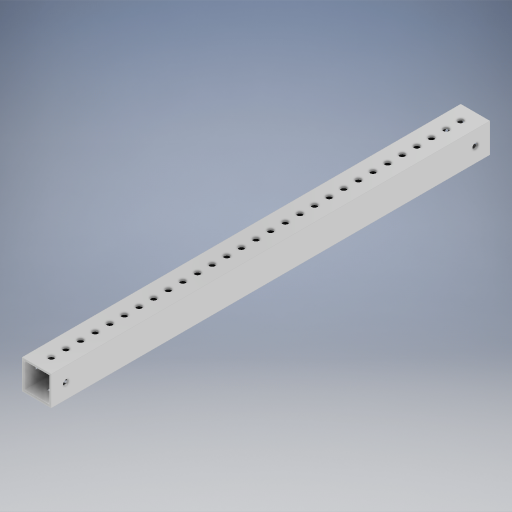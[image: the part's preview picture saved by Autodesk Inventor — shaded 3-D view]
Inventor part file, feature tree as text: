
AUTODESK INVENTOR PART (.ipt)
format: ipt  version: 2024.2 (Build 282272000, 272)  size: 795,136 bytes
history: native  units: in
note: dims shown in document units (in); Inventor stores cm internally (conversion verified against a paired STEP export)
features: other x13, extrude x9, hole x3, pattern_linear x3, mirror x3, sheet_metal_op x1, plane x1
ambient origin geometry x8: Origin, YZ Plane, XZ Plane, XY Plane, X Axis, Y Axis, Z Axis, Center Point
bodies: Solid1 (feature_tree)
feature tree (33):
  other  "Blocks"
  other  "Base Sketch"
  extrude  "Base"  Depth=1.0in
  extrude  "MAX Corner"  Depth=1.0in
  extrude  "MAX Corner Cut"  Depth=0.0625in
  extrude  "Scribe Lines"  Depth=0.0625in
  other  "Side Middle"
  other  "Top Middle"
  other  "Side Holes Sketch"
  hole  "Top Side Hole"  [1 undecoded]
  hole  "Mid Side Hole"  [1 undecoded]
  hole  "Btm Side Hole"  [1 undecoded]
  pattern_linear  "Side Holes"  Spacing1=0.04in  [1 undecoded]
  mirror  "Side Mirror"
  extrude  "MAXTube Hole"  Depth=0.04in
  extrude  "MAXTube Outside"  Depth=15.0in
  pattern_linear  "MAXTube Pattern"  Spacing1=0.0in  [1 undecoded]
  mirror  "MAXTube Mirror"
  extrude  "Left Top Hole"  Depth=15.0in
  extrude  "Mid Top Hole"  TaperAngle=0.0deg  [1 undecoded]
  extrude  "Right Top Hole"  TaperAngle=0.0deg  [1 undecoded]
  pattern_linear  "Top Holes"  Spacing1=0.005in  [1 undecoded]
  mirror  "Top Mirror"
  sheet_metal_op  "Corner"
  other  "MAXTube"
  plane  "Work Plane3"
  other  "Corner:5"
  other  "Corner:6"
  other  "Corner:7"
  other  "Corner:8"
  other  "MAXTube:1"
  other  "MAXTube:2"
  other  "MAXTube:3"
note: 8 required parameter values undecoded (feature->parameter linkage not recoverable at this tier; creation-order binding heuristic only, values carry confidence <= 0.55)
